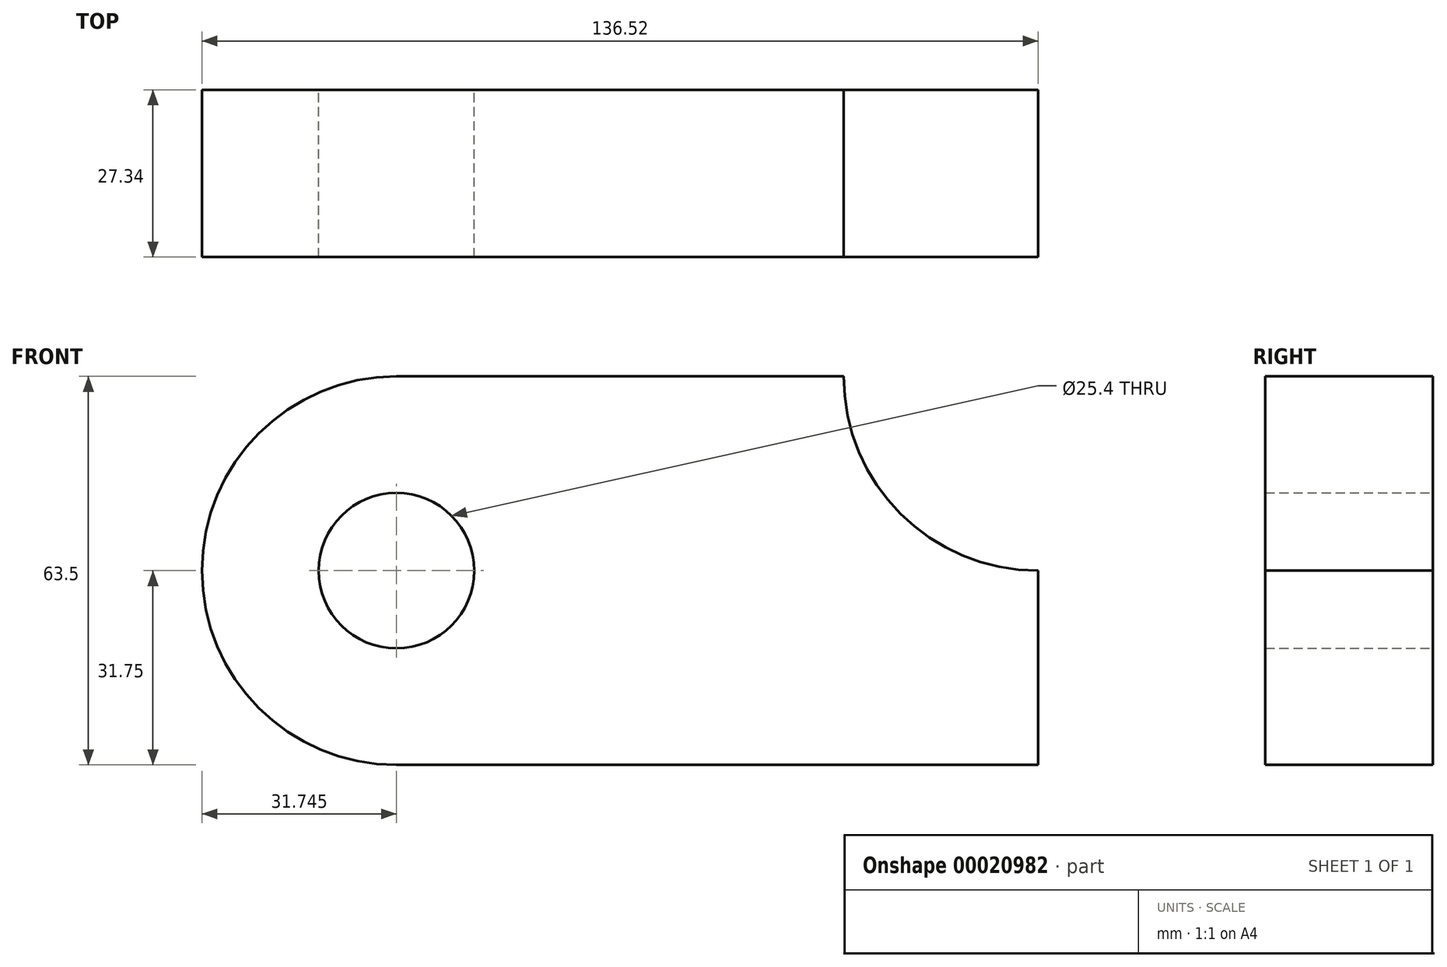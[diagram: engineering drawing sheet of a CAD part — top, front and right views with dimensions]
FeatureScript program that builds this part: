
annotation { "Feature Type Name" : "Feature", "Feature Type Description" : "" }
export const myFeature = defineFeature(function(context is Context, id is Id, definition is map)
    precondition{}
    {
        {
            var Q0;
            Q0=qCreatedBy(makeId("Front.planeOp"),FACE);
            var sketch = newSketch(context, id + "F0", { "sketchPlane" : qUnion([Q0])});
            skLineSegment(sketch, "E0.bottom", {"start": v(0, 0) * mm, "end": v(-104.77, 0) * mm});
            skLineSegment(sketch, "E0.top", {"start": v(-31.75, 63.5) * mm, "end": v(-104.78, 63.5) * mm});
            skLineSegment(sketch, "E0.left", {"start": v(0, 0) * mm, "end": v(0, 31.75) * mm});
            skArc(sketch, "E1", {"start": v(-104.78, 63.5) * mm, "mid": v(-136.53, 31.75) * mm, "end": v(-104.77, 0) * mm});
            skCircle(sketch, "E2", {"center": v(-104.78, 31.75) * mm, "radius": 12.7 * mm});
            skArc(sketch, "E3", {"start": v(-31.75, 63.5) * mm, "mid": v(-22.45, 41.05) * mm, "end": v(0, 31.75) * mm});
            skSolve(sketch);
        }
        {
            var Q0;
            Q0=makeQuery(id+"F0.imprint","IMPRINT",FACE,{"disambiguationData":[TD([[makeQuery(id+"F0.imprint","IMPRINT",EDGE,{"derivedFrom":sQuery(id+"F0.wireOp",EDGE,"E0.bottom")}),-1.0]])]});
            extrude(context, id + "F1", {"entities" : qUnion([Q0]), "depth" : 27.34 * mm});
        }
    });
